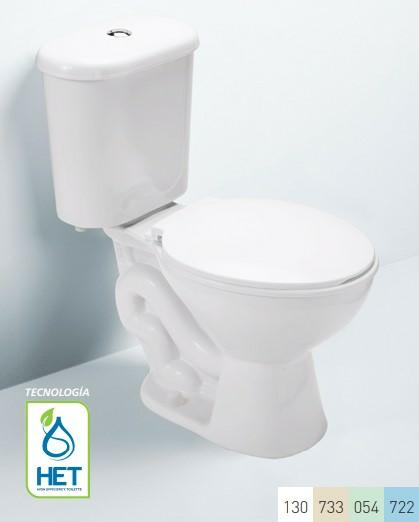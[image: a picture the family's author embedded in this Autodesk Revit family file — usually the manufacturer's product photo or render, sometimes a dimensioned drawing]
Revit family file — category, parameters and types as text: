
# Revit family: BRG-GRF-DCH_BELA DUCHA DE MANO CROMO v02
name_source: partatom
category: Aparatos sanitarios
units: mm (PartAtom-declared; Revit-internal decimal feet)

## family parameters
Anfitrión = Muro
Compartido = No
Corte con vacíos al cargar = No
Cota de conector redondo = Diámetro de uso
Número OmniClass = 23.45.00.00
Punto de cálculo de habitación = No
Siempre vertical = Sí
Tipo de pieza = Normal
Título OmniClass = Sanitary, Laundry, and Cleaning Equipment

## types (1)
- BELA DUCHA TELÉFONO
    Fabricante = BRIGGS Ecuador
    Modelo = BELA DUCHA TELÉFONO
    URL = https://www.briggs.com.ec
    _ALT_ LLave = 0.8 m
    _ALT_ Montaje = 1.5 m
    _EDESA_ Alto en cm = 5
    _EDESA_ Ancho en cm = 5
    _EDESA_ Categoría = Productos > Grifería > Ducha
    _EDESA_ Certificación = Cumple con norma NTE - INEN 3123 basada en la norma ASME 112.18.1 - 2012.
    _EDESA_ Color = Cromo
    _EDESA_ Conexión hidráulica = Entrada de agua: tubería ø 1/2"
    _EDESA_ Consumo/capacidad de agua en L = 9.5 litros por minuto / 2.5 gpm
    _EDESA_ Descripción = Grifería ducha teléfono. Instalación externa a la pared. Incluye soporte, manguera flexible y regadera de mano.
    _EDESA_ Garantía = De por vida para el cuerpo principal y acabado en cromo (306)
    _EDESA_ Manual de instalación = https://www.briggs.com.ec
    _EDESA_ Marca = BRIGGS
    _EDESA_ Materiales = Latón
    _EDESA_ Nombre = BELA DUCHA TELÉFONO
    _EDESA_ Productos necesarios para instalación = Mezcladora de ducha
    _EDESA_ Profundidad en cm = 3
    _EDESA_ Sku/código = SG0087123061CW
    _EDESA_ Tipo de instalación = A la pared
